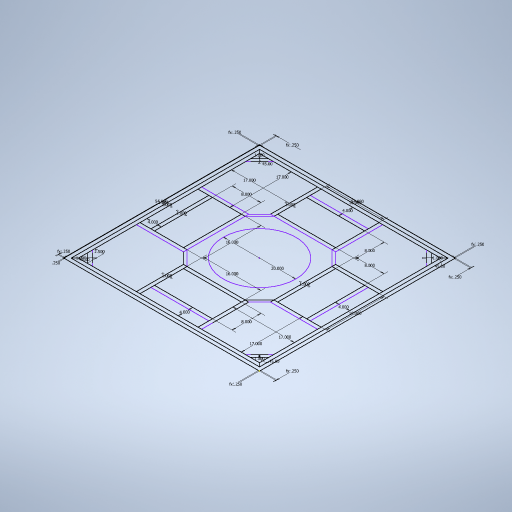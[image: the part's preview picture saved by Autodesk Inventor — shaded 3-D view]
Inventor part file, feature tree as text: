
AUTODESK INVENTOR PART (.ipt)
format: ipt  version: 2023 (Build 270158000, 158)  size: 309,248 bytes
history: native  units: in
note: dims shown in document units (in); Inventor stores cm internally (conversion verified against a paired STEP export)
features: sketch x1
ambient origin geometry x8: Origin, YZ Plane, XZ Plane, XY Plane, X Axis, Y Axis, Z Axis, Center Point
feature tree (1):
  sketch  "Sketch1"  dims[d0=54.0in d1=54.0in d2=1.0in d3=1.0in d4=8.0in d5=16.0in d6=8.0in d7=16.0in d8=16.0in d9=8.0in d10=16.0in d11=8.0in d12=4.0in d13=4.0in d14=4.0in d15=4.0in d16=17.0in d17=17.0in d18=17.0in d19=17.0in d20=20.0in d21=1.0in d22=1.0in d23=1.0in d24=1.0in d25=45.0deg d26=2.5in d27=45.0deg d28=45.0deg d29=45.0deg d30=1.0in d31=1.0in d32=1.0in d33=1.0in d34=0.25in d35=0.25in d36=0.25in d37=0.25in d38=0.25in d39=0.25in d40=0.25in d41=0.25in]
